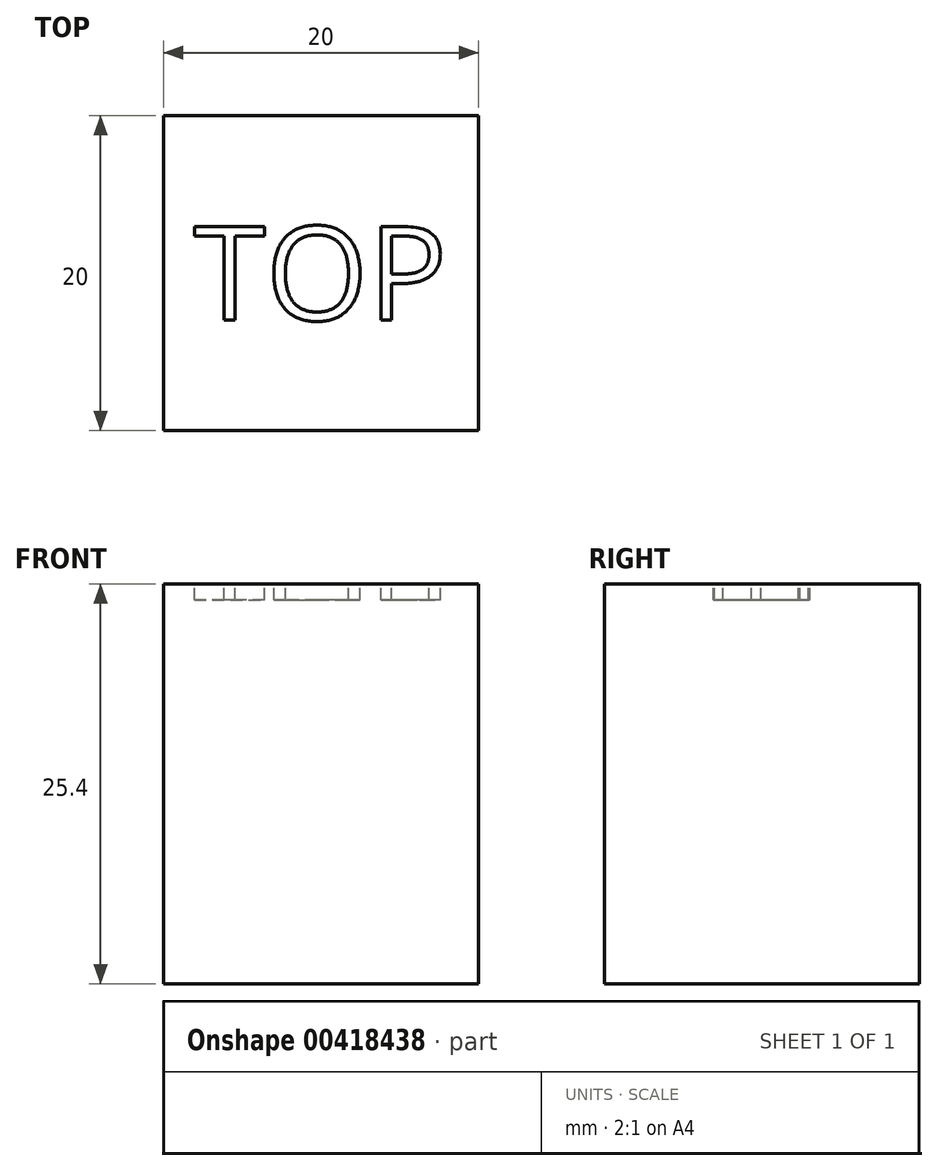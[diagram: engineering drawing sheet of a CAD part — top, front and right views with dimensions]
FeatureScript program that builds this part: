
annotation { "Feature Type Name" : "Feature", "Feature Type Description" : "" }
export const myFeature = defineFeature(function(context is Context, id is Id, definition is map)
    precondition{}
    {
        {
            var Q0;
            Q0=qCreatedBy(makeId("Top.planeOp"),FACE);
            var sketch = newSketch(context, id + "F0", { "sketchPlane" : qUnion([Q0])});
            skLineSegment(sketch, "E0.bottom", {"start": v(-10, -10) * mm, "end": v(10, -10) * mm});
            skLineSegment(sketch, "E0.top", {"start": v(-10, 10) * mm, "end": v(10, 10) * mm});
            skLineSegment(sketch, "E0.left", {"start": v(-10, -10) * mm, "end": v(-10, 10) * mm});
            skLineSegment(sketch, "E0.right", {"start": v(10, -10) * mm, "end": v(10, 10) * mm});
            skSolve(sketch);
        }
        {
            var Q0;
            Q0 = qSketchRegion(id + "F0", true);
            extrude(context, id + "F1", {"entities" : qUnion([Q0]), "depth" : 25.4 * mm});
        }
        {
            var Q0;
            Q0=makeQuery(id+"F1.opExtrude","CAP_FACE",FACE,{"disambiguationData":[OSD([sQuery(id+"F0.wireOp",EDGE,"E0.bottom"),sQuery(id+"F0.wireOp",EDGE,"E0.top"),sQuery(id+"F0.wireOp",EDGE,"E0.left"),sQuery(id+"F0.wireOp",EDGE,"E0.right")])],"isStart":false});
            var sketch = newSketch(context, id + "F2", { "sketchPlane" : qUnion([Q0])});
            skText(sketch, "E1", { "text": "TOP", "fontName": "OpenSans-Regular.ttf"});
            const initialGuessF2  = {"E1": [-0.00812, -0.003, 1, 0, 0.006]};
            skSetInitialGuess(sketch, initialGuessF2);
            skSolve(sketch);
        }
        {
            var Q0;
            Q0 = qSketchRegion(id + "F2", true);
            extrude(context, id + "F3", {"entities" : qUnion([Q0]), "operationType" : NewBodyOperationType.REMOVE, "oppositeDirection" : true, "depth" : 1 * mm});
        }
    });
